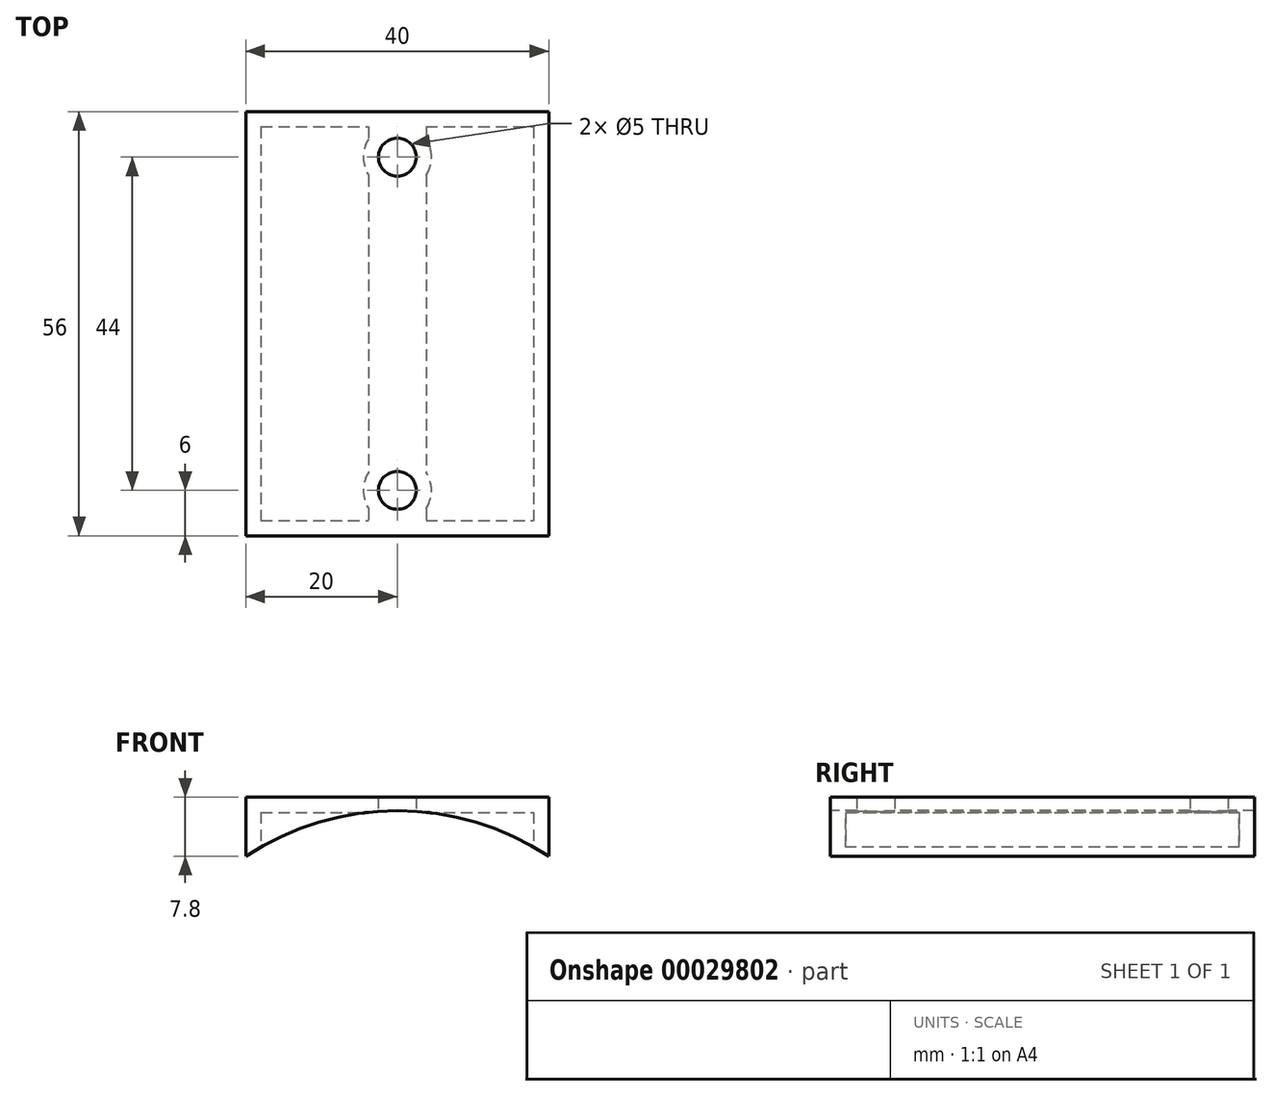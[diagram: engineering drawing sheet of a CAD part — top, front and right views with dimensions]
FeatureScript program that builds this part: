
annotation { "Feature Type Name" : "Feature", "Feature Type Description" : "" }
export const myFeature = defineFeature(function(context is Context, id is Id, definition is map)
    precondition{}
    {
        {
            var Q0;
            Q0=qCreatedBy(makeId("Top.planeOp"),FACE);
            var sketch = newSketch(context, id + "F0", { "sketchPlane" : qUnion([Q0])});
            skLineSegment(sketch, "E0.bottom", {"start": v(0, 0) * mm, "end": v(40, 0) * mm});
            skLineSegment(sketch, "E0.top", {"start": v(0, 56) * mm, "end": v(40, 56) * mm});
            skLineSegment(sketch, "E0.left", {"start": v(0, 0) * mm, "end": v(0, 56) * mm});
            skLineSegment(sketch, "E0.right", {"start": v(40, 0) * mm, "end": v(40, 56) * mm});
            skLineSegment(sketch, "E1.0", {"start": v(0, 50) * mm, "end": v(40, 50) * mm, "construction": true});
            skLineSegment(sketch, "E2.0", {"start": v(0, 6) * mm, "end": v(40, 6) * mm, "construction": true});
            skCircle(sketch, "E3", {"center": v(20, 50) * mm, "radius": 2.5 * mm});
            skCircle(sketch, "E4", {"center": v(20, 6) * mm, "radius": 2.5 * mm});
            skSolve(sketch);
        }
        {
            var Q0;
            Q0 = qSketchRegion(id + "F0", true);
            extrude(context, id + "F1", {"entities" : qUnion([Q0]), "depth" : 7.8 * mm});
        }
        {
            var Q0;
            Q0=makeQuery(id+"F1.opExtrude","SWEPT_FACE",FACE,{"disambiguationData":[OSD([sQuery(id+"F0.wireOp",EDGE,"E0.bottom")])]});
            var sketch = newSketch(context, id + "F2", { "sketchPlane" : qUnion([Q0])});
            skArc(sketch, "E5", {"start": v(40, 0) * mm, "mid": v(20, 6) * mm, "end": v(0, 0) * mm});
            skLineSegment(sketch, "E6", {"start": v(0, 0) * mm, "end": v(40, 0) * mm});
            skSolve(sketch);
        }
        {
            var Q0;
            Q0 = qSketchRegion(id + "F2", true);
            var Q1;
            Q1=makeQuery(id+"F2.imprint","IMPRINT",FACE,{"disambiguationData":[TD([[makeQuery(id+"F2.imprint","IMPRINT",EDGE,{"derivedFrom":sQuery(id+"F2.wireOp",EDGE,"b04a92b5-6d0f-442e-b2f7-7dad052b3aea")}),1.0]])]});
            extrude(context, id + "F3", {"entities" : qUnion([Q0, Q1]), "operationType" : NewBodyOperationType.REMOVE, "oppositeDirection" : true, "depth" : 100 * mm});
        }
        {
            var Q0;
            Q0=makeQuery(id+"F3.boolean.opBoolean","COPY",FACE,{"derivedFrom":makeQuery(id+"F3.opExtrude","SWEPT_FACE",FACE,{"disambiguationData":[OSD([sQuery(id+"F2.wireOp",EDGE,"E5")])]})});
            shell(context, id + "F4", {"entities" : qUnion([Q0]), "thickness" : 2 * mm});
        }
    });
